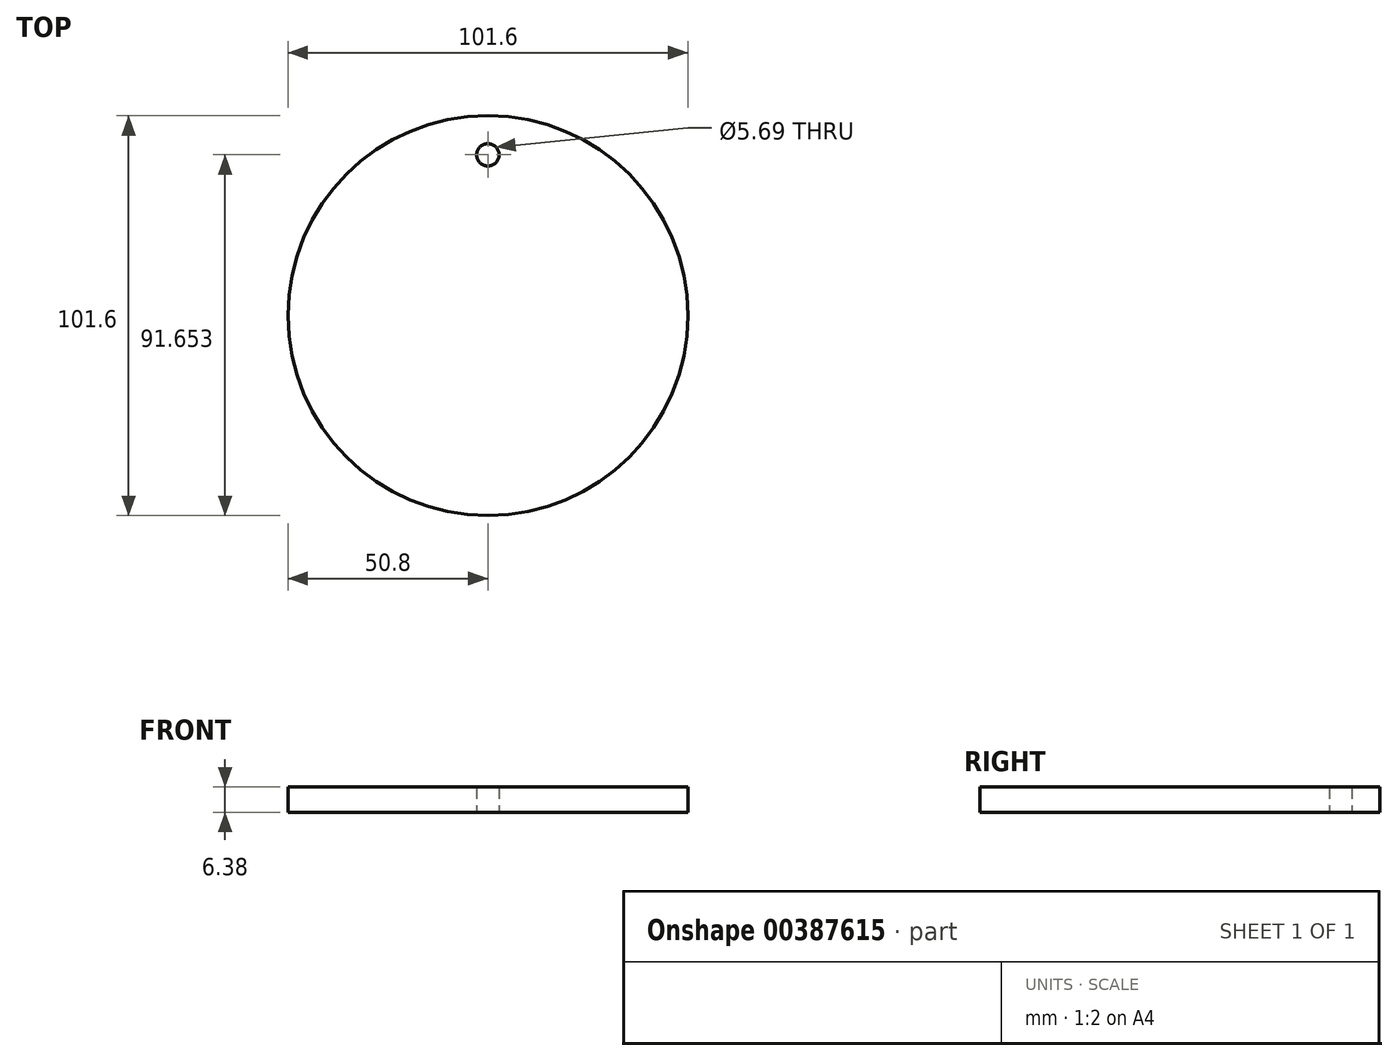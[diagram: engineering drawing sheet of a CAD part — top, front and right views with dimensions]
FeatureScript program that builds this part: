
annotation { "Feature Type Name" : "Feature", "Feature Type Description" : "" }
export const myFeature = defineFeature(function(context is Context, id is Id, definition is map)
    precondition{}
    {
        {
            var Q0;
            Q0=qCreatedBy(makeId("Top.planeOp"),FACE);
            var sketch = newSketch(context, id + "F0", { "sketchPlane" : qUnion([Q0])});
            skCircle(sketch, "E0", {"center": v(0, 0) * mm, "radius": 50.8 * mm});
            skCircle(sketch, "E1", {"center": v(0, 40.85) * mm, "radius": 2.84 * mm});
            skSolve(sketch);
        }
        {
            var Q0;
            Q0 = qSketchRegion(id + "F0", true);
            extrude(context, id + "F1", {"entities" : qUnion([Q0]), "depth" : 6.38 * mm});
        }
    });
